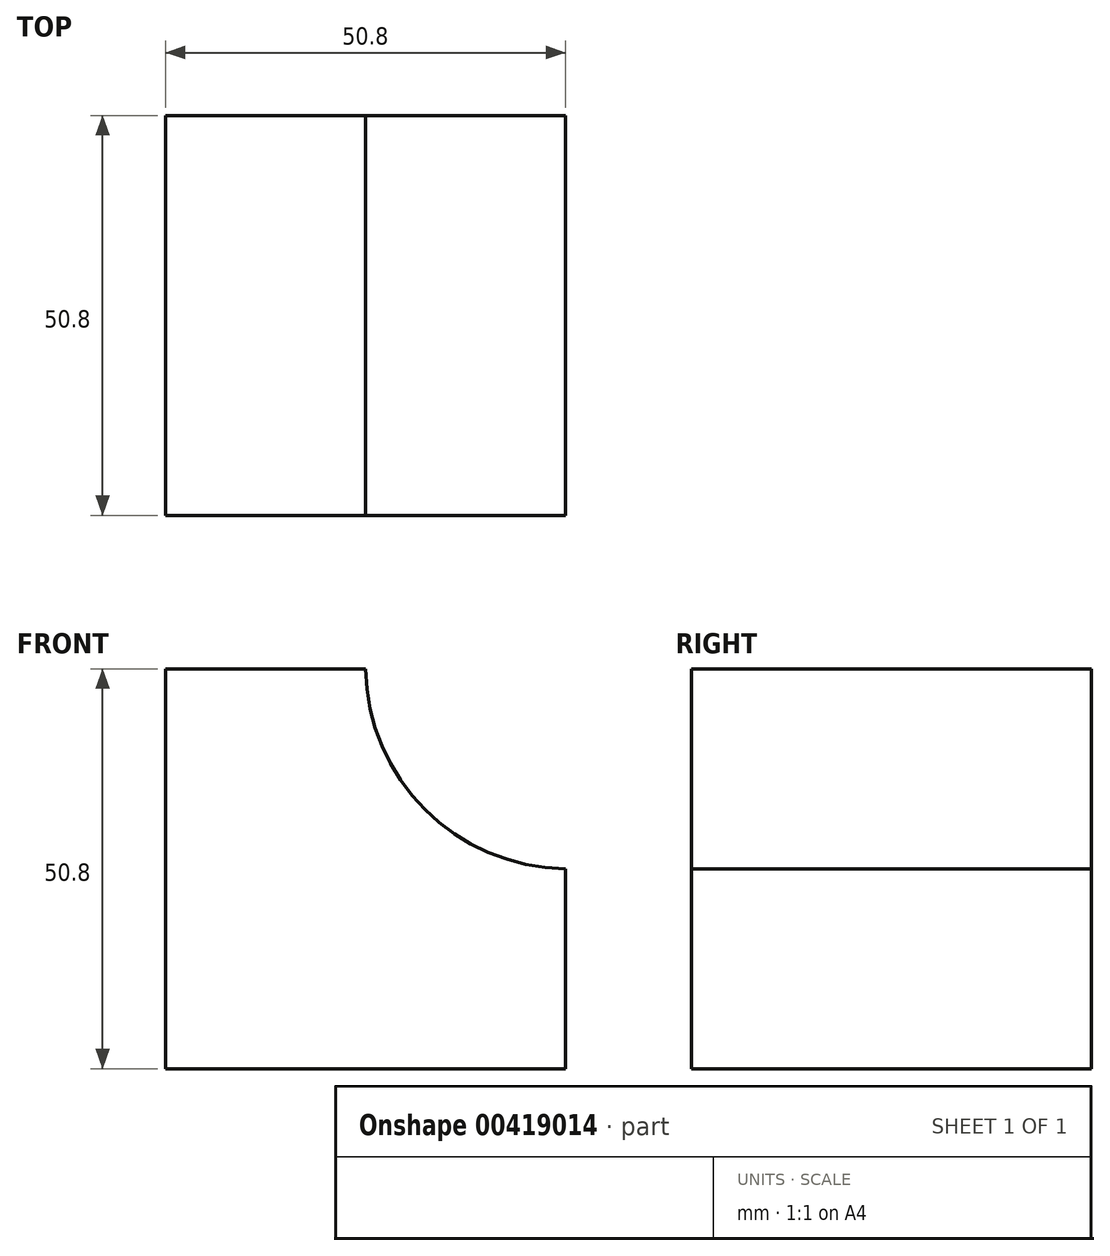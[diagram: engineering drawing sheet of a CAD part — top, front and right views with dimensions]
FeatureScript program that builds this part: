
annotation { "Feature Type Name" : "Feature", "Feature Type Description" : "" }
export const myFeature = defineFeature(function(context is Context, id is Id, definition is map)
    precondition{}
    {
        {
            var Q0;
            Q0=qCreatedBy(makeId("Front.planeOp"),FACE);
            var sketch = newSketch(context, id + "F0", { "sketchPlane" : qUnion([Q0])});
            skLineSegment(sketch, "E0", {"start": v(0, 25.4) * mm, "end": v(0, 0) * mm});
            skLineSegment(sketch, "E1", {"start": v(0, 0) * mm, "end": v(-50.8, 0) * mm});
            skLineSegment(sketch, "E2", {"start": v(-50.8, 0) * mm, "end": v(-50.8, 50.8) * mm});
            skLineSegment(sketch, "E3", {"start": v(-50.8, 50.8) * mm, "end": v(-25.4, 50.8) * mm});
            skArc(sketch, "E4", {"start": v(-25.4, 50.8) * mm, "mid": v(-17.86, 32.94) * mm, "end": v(0, 25.4) * mm});
            skSolve(sketch);
        }
        {
            var Q0;
            Q0=makeQuery(id+"F0.imprint","IMPRINT",FACE,{"disambiguationData":[TD([[makeQuery(id+"F0.imprint","IMPRINT",EDGE,{"derivedFrom":sQuery(id+"F0.wireOp",EDGE,"E0")}),-1.0]])]});
            extrude(context, id + "F1", {"entities" : qUnion([Q0]), "depth" : 50.8 * mm});
        }
    });
